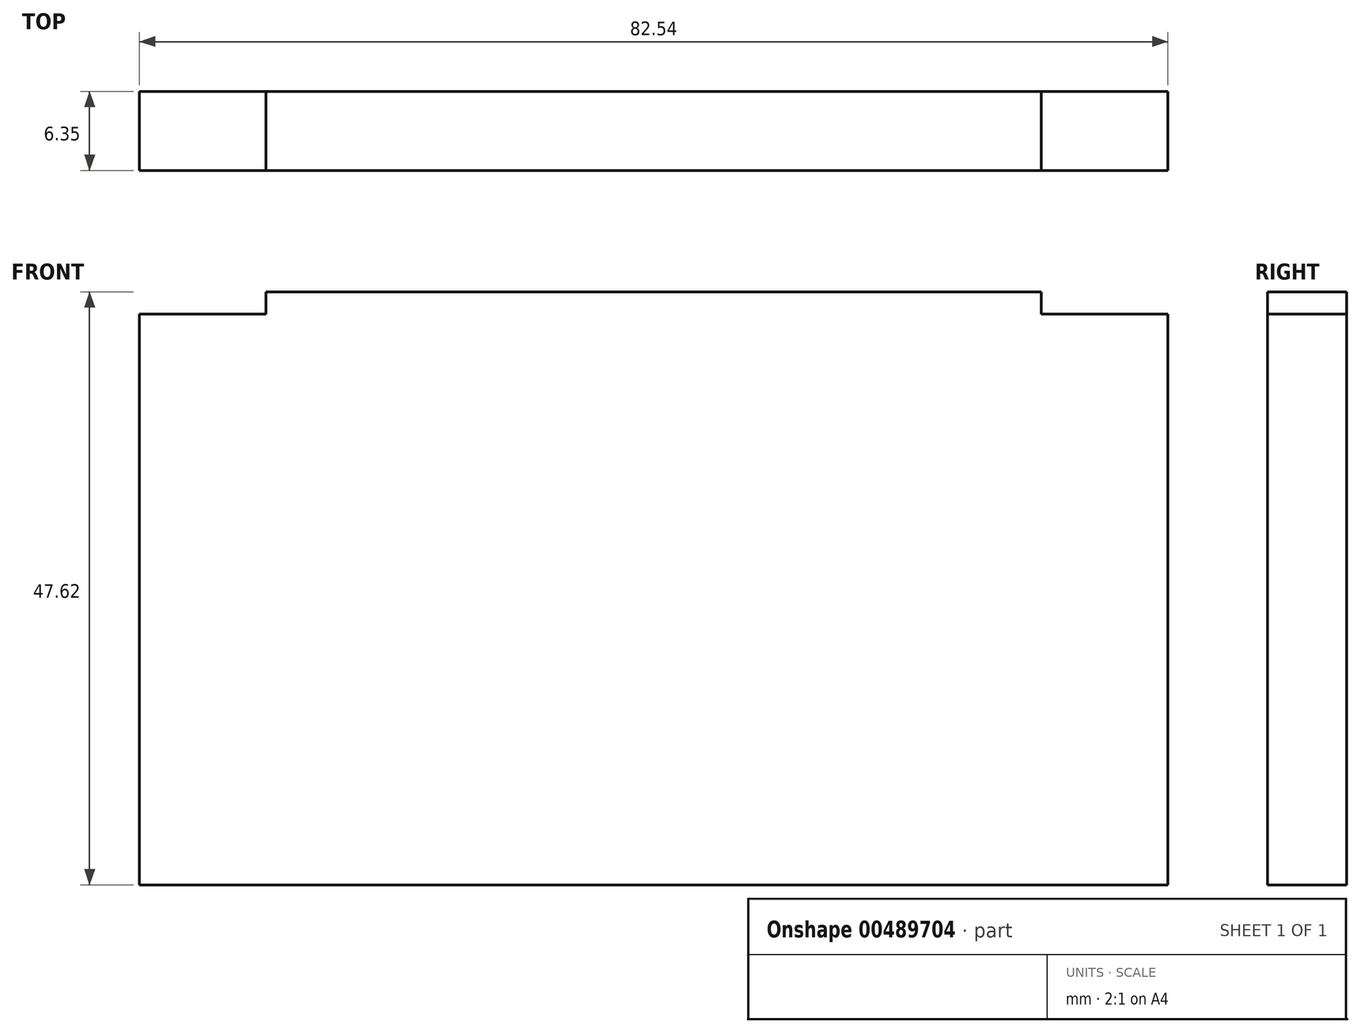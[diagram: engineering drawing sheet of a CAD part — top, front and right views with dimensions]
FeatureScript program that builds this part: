
annotation { "Feature Type Name" : "Feature", "Feature Type Description" : "" }
export const myFeature = defineFeature(function(context is Context, id is Id, definition is map)
    precondition{}
    {
        {
            var Q0;
            Q0=qCreatedBy(makeId("Front.planeOp"),FACE);
            var sketch = newSketch(context, id + "F0", { "sketchPlane" : qUnion([Q0])});
            skLineSegment(sketch, "E0.bottom", {"start": v(31.12, 23.81) * mm, "end": v(-31.12, 23.81) * mm});
            skLineSegment(sketch, "E0.top", {"start": v(41.28, -23.81) * mm, "end": v(-41.27, -23.81) * mm});
            skLineSegment(sketch, "E0.left", {"start": v(41.28, 22.03) * mm, "end": v(41.28, -23.81) * mm});
            skLineSegment(sketch, "E0.right", {"start": v(-41.28, 22.03) * mm, "end": v(-41.27, -23.81) * mm});
            skPoint(sketch, "E0.middle", {"position": v(0, 0) * mm});
            skLineSegment(sketch, "E1.top", {"start": v(-41.28, 22.03) * mm, "end": v(-31.12, 22.03) * mm});
            skLineSegment(sketch, "E1.right", {"start": v(-31.12, 23.81) * mm, "end": v(-31.12, 22.03) * mm});
            skLineSegment(sketch, "E2.MirrorCS", {"start": v(41.28, 22.03) * mm, "end": v(31.12, 22.03) * mm});
            skLineSegment(sketch, "E3.MirrorCS", {"start": v(31.12, 23.81) * mm, "end": v(31.12, 22.03) * mm});
            skPoint(sketch, "E4.orphan", {"position": v(-41.28, 23.81) * mm});
            skPoint(sketch, "E5.orphan", {"position": v(41.28, 23.81) * mm});
            skSolve(sketch);
        }
        {
            var Q0;
            Q0 = qSketchRegion(id + "F0", true);
            extrude(context, id + "F1", {"entities" : qUnion([Q0]), "depth" : 6.35 * mm});
        }
    });
